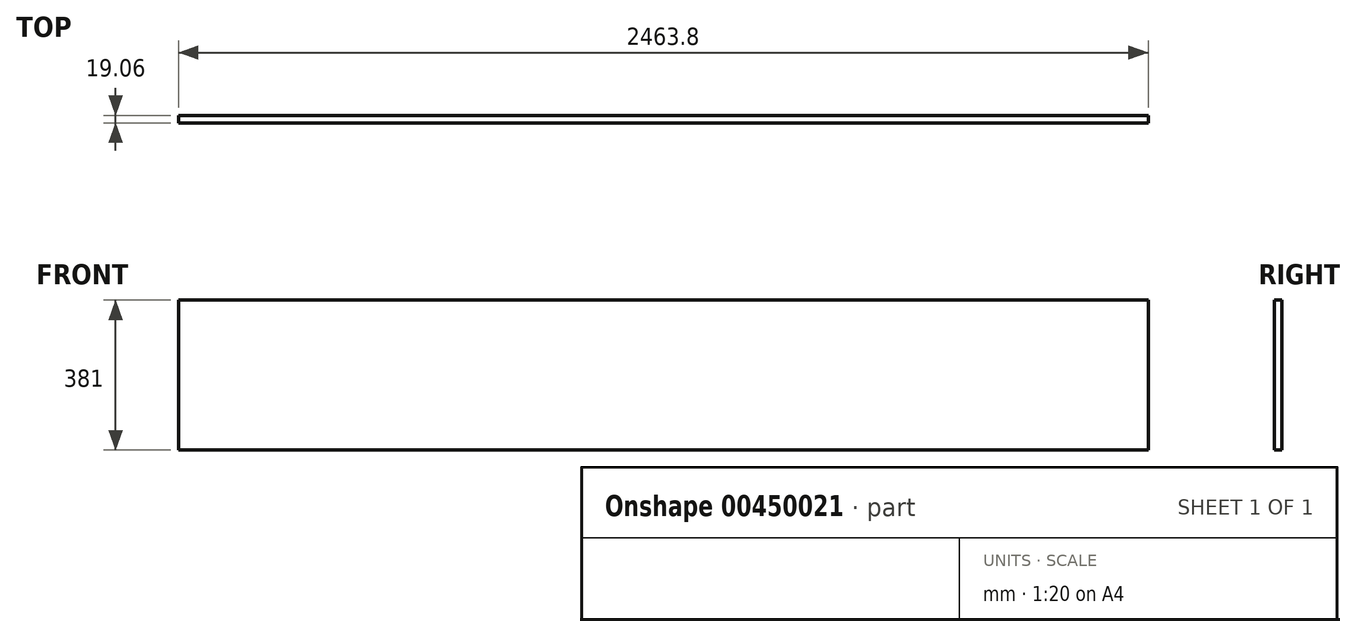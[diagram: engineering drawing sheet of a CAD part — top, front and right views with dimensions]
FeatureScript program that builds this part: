
annotation { "Feature Type Name" : "Feature", "Feature Type Description" : "" }
export const myFeature = defineFeature(function(context is Context, id is Id, definition is map)
    precondition{}
    {
        {
            var Q0;
            Q0=qCreatedBy(makeId("Front.planeOp"),FACE);
            var sketch = newSketch(context, id + "F0", { "sketchPlane" : qUnion([Q0])});
            skLineSegment(sketch, "E0", {"start": v(0, 0) * mm, "end": v(0, 61.28) * mm, "construction": true});
            skLineSegment(sketch, "E1", {"start": v(0, 0) * mm, "end": v(103.55, 0) * mm, "construction": true});
            skLineSegment(sketch, "E2.bottom", {"start": v(0, 190.5) * mm, "end": v(2463.8, 190.5) * mm});
            skLineSegment(sketch, "E2.top", {"start": v(0, -190.5) * mm, "end": v(2463.8, -190.5) * mm});
            skLineSegment(sketch, "E2.left", {"start": v(0, 190.5) * mm, "end": v(0, -190.5) * mm});
            skLineSegment(sketch, "E2.right", {"start": v(2463.8, 190.5) * mm, "end": v(2463.8, -190.5) * mm});
            skSolve(sketch);
        }
        {
            var Q0;
            Q0=makeQuery(id+"F0.imprint","IMPRINT",FACE,{"disambiguationData":[TD([[makeQuery(id+"F0.imprint","IMPRINT",EDGE,{"derivedFrom":sQuery(id+"F0.wireOp",EDGE,"E2.bottom")}),-1.0]])]});
            extrude(context, id + "F1", {"entities" : qUnion([Q0]), "endBound" : BoundingType.SYMMETRIC, "depth" : 19.05 * mm});
        }
    });
